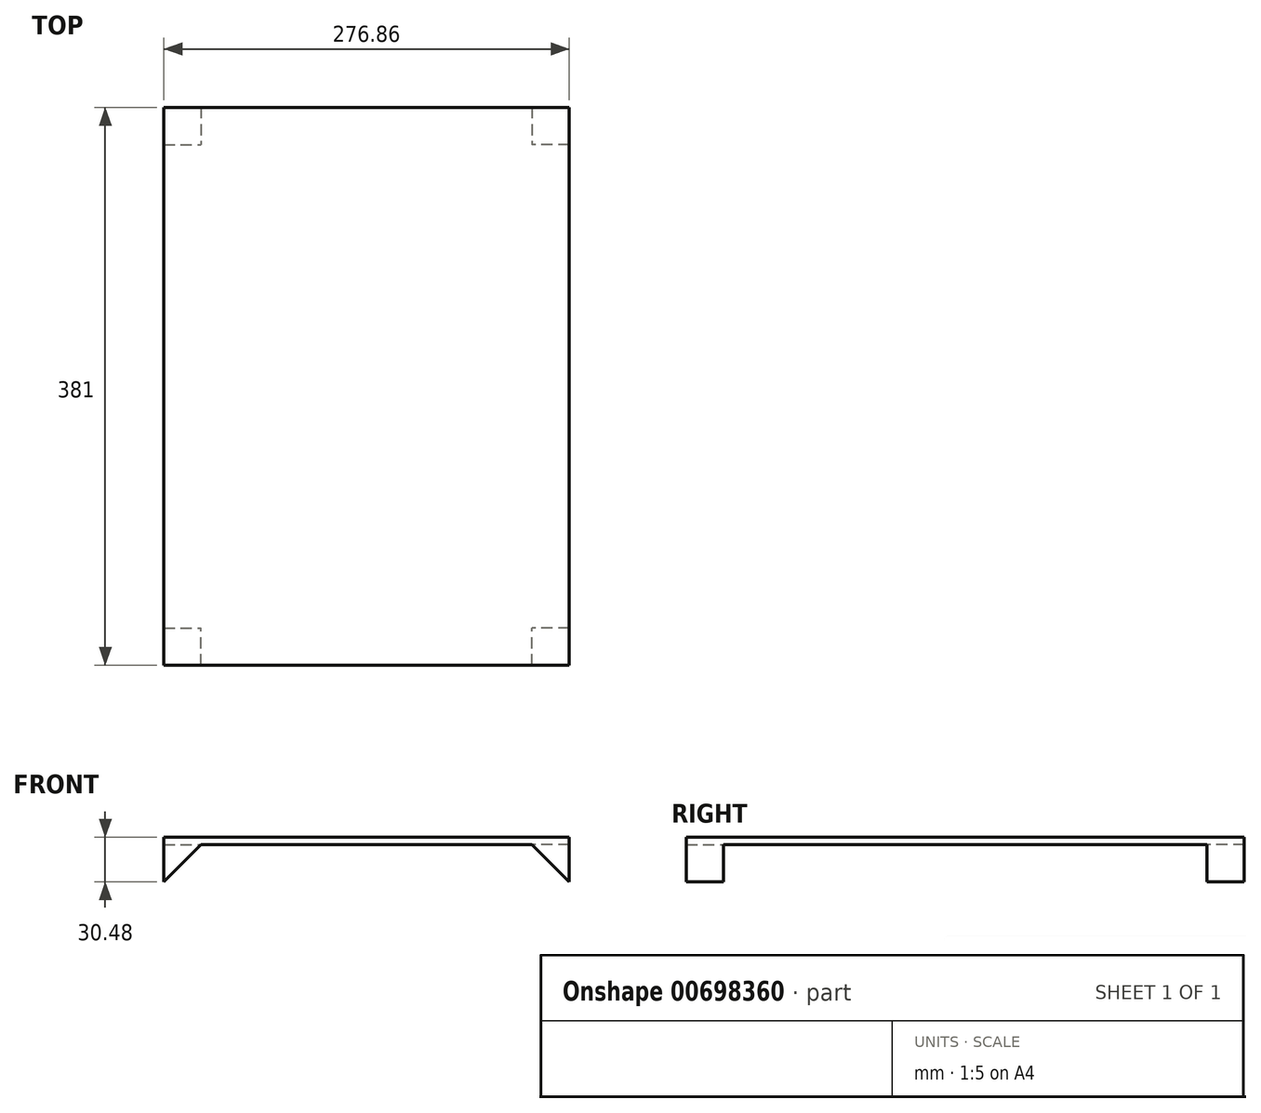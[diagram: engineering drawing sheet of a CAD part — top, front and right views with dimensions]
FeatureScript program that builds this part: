
annotation { "Feature Type Name" : "Feature", "Feature Type Description" : "" }
export const myFeature = defineFeature(function(context is Context, id is Id, definition is map)
    precondition{}
    {
        {
            var Q0;
            Q0=qCreatedBy(makeId("Front.planeOp"),FACE);
            var sketch = newSketch(context, id + "F0", { "sketchPlane" : qUnion([Q0])});
            skLineSegment(sketch, "E0.bottom", {"start": v(-138.43, 2.54) * mm, "end": v(138.43, 2.54) * mm});
            skLineSegment(sketch, "E0.top", {"start": v(-138.43, -2.54) * mm, "end": v(138.43, -2.54) * mm});
            skLineSegment(sketch, "E0.left", {"start": v(-138.43, 2.54) * mm, "end": v(-138.43, -2.54) * mm});
            skLineSegment(sketch, "E0.right", {"start": v(138.43, 2.54) * mm, "end": v(138.43, -2.54) * mm});
            skPoint(sketch, "E0.middle", {"position": v(0, 0) * mm});
            skSolve(sketch);
        }
        {
            var Q0;
            Q0 = qSketchRegion(id + "F0", true);
            extrude(context, id + "F1", {"entities" : qUnion([Q0]), "depth" : 381 * mm, "offsetDistance" : 25.4 * mm});
        }
        {
            var Q0;
            Q0=makeQuery(id+"F1.opExtrude","SWEPT_FACE",FACE,{"disambiguationData":[OSD([sQuery(id+"F0.wireOp",EDGE,"E0.top")])]});
            var sketch = newSketch(context, id + "F2", { "sketchPlane" : qUnion([Q0])});
            skLineSegment(sketch, "E1.bottom", {"start": v(138.43, 381) * mm, "end": v(113.03, 381) * mm});
            skLineSegment(sketch, "E1.top", {"start": v(138.43, 355.6) * mm, "end": v(113.03, 355.6) * mm});
            skLineSegment(sketch, "E1.left", {"start": v(138.43, 381) * mm, "end": v(138.43, 355.6) * mm});
            skLineSegment(sketch, "E1.right", {"start": v(113.03, 381) * mm, "end": v(113.03, 355.6) * mm});
            skLineSegment(sketch, "E2.bottom", {"start": v(-138.43, 381) * mm, "end": v(-113.03, 381) * mm});
            skLineSegment(sketch, "E2.top", {"start": v(-138.43, 355.6) * mm, "end": v(-113.03, 355.6) * mm});
            skLineSegment(sketch, "E2.left", {"start": v(-138.43, 381) * mm, "end": v(-138.43, 355.6) * mm});
            skLineSegment(sketch, "E2.right", {"start": v(-113.03, 381) * mm, "end": v(-113.03, 355.6) * mm});
            skLineSegment(sketch, "E3.bottom", {"start": v(-138.43, 0) * mm, "end": v(-113.03, 0) * mm});
            skLineSegment(sketch, "E3.top", {"start": v(-138.43, 25.4) * mm, "end": v(-113.03, 25.4) * mm});
            skLineSegment(sketch, "E3.left", {"start": v(-138.43, 0) * mm, "end": v(-138.43, 25.4) * mm});
            skLineSegment(sketch, "E3.right", {"start": v(-113.03, 0) * mm, "end": v(-113.03, 25.4) * mm});
            skLineSegment(sketch, "E4.bottom", {"start": v(138.43, 0) * mm, "end": v(113.03, 0) * mm});
            skLineSegment(sketch, "E4.top", {"start": v(138.43, 25.4) * mm, "end": v(113.03, 25.4) * mm});
            skLineSegment(sketch, "E4.left", {"start": v(138.43, 0) * mm, "end": v(138.43, 25.4) * mm});
            skLineSegment(sketch, "E4.right", {"start": v(113.03, 0) * mm, "end": v(113.03, 25.4) * mm});
            skSolve(sketch);
        }
        {
            var Q0;
            Q0 = qSketchRegion(id + "F2", true);
            extrude(context, id + "F3", {"entities" : qUnion([Q0]), "operationType" : NewBodyOperationType.ADD, "depth" : 25.4 * mm, "offsetDistance" : 25.4 * mm});
        }
        {
            var Q0;
            Q0=makeQuery(id+"F3.opExtrude","CAP_EDGE",EDGE,{"disambiguationData":[OSD([sQuery(id+"F2.wireOp",EDGE,"E2.right")])],"isStart":false});
            chamfer(context, id + "F4", {"entities" : qUnion([Q0]), "width" : 25.4 * mm, "tangentPropagation" : true});
        }
        {
            var Q0;
            Q0=makeQuery(id+"F3.opExtrude","CAP_EDGE",EDGE,{"disambiguationData":[OSD([sQuery(id+"F2.wireOp",EDGE,"E1.right")])],"isStart":false});
            var Q1;
            Q1=makeQuery(id+"F3.opExtrude","CAP_EDGE",EDGE,{"disambiguationData":[OSD([sQuery(id+"F2.wireOp",EDGE,"E4.right")])],"isStart":false});
            var Q2;
            Q2=makeQuery(id+"F3.opExtrude","CAP_EDGE",EDGE,{"disambiguationData":[OSD([sQuery(id+"F2.wireOp",EDGE,"E3.right")])],"isStart":false});
            chamfer(context, id + "F5", {"entities" : qUnion([Q0, Q1, Q2]), "width" : 25.4 * mm, "tangentPropagation" : true});
        }
    });
